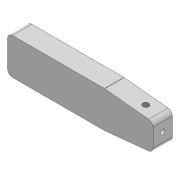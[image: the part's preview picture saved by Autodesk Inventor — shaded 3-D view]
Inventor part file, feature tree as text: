
AUTODESK INVENTOR PART (.ipt)
format: ipt  version: 2018 (Build 220112000, 112)  size: 128,512 bytes
history: native  units: mm
features: sketch x4, extrude x2, hole x2, projected_geometry x2, mirror x1, fillet x1
ambient origin geometry x8: Origin, YZ Plane, XZ Plane, XY Plane, X Axis, Y Axis, Z Axis, Center Point
bodies: Solid1 (feature_tree)
feature tree (12):
  extrude  "Extrusion1"  Depth=60.0mm
  extrude  "Extrusion2"  Depth=20.0mm
  mirror  "Mirror1"
  fillet  "Fillet1"  Radius=2.0mm
  hole  "Hole1"  [1 undecoded]
  hole  "Hole2"  [1 undecoded]
  sketch  "Sketch1"  dims[d0=15.0mm d1=60.0mm]
  sketch  "Sketch2"  dims[d2=8.0mm d3=0.0mm d4=20.0mm d5=2.0mm]
  projected_geometry  "Projected Loop1"
  sketch  "Sketch3"  dims[d6=3.0mm d7=0.0mm d8=2.0mm]
  projected_geometry  "Projected Loop2"
  sketch  "Sketch4"  dims[d9=2.0mm d10=6.0mm d11=4.0mm d12=2.0mm d13=90.0deg d14=8.0mm d15=20.594885mm d16=7.0mm d17=2.459mm d18=10.0mm d19=4.0mm d20=2.0mm d21=90.0deg d22=8.8mm d23=20.594885mm]
note: 2 required parameter values undecoded (feature->parameter linkage not recoverable at this tier; creation-order binding heuristic only, values carry confidence <= 0.55)
